# Revit family: SW17 TETT
name_source: partatom
category: Detail Items
units: mm (PartAtom-declared; Revit-internal decimal feet)

## family parameters
Rotate with component = No
Section Shape = Not Defined
Shared = No

## types (5) — shared parameters
URL = www.superwood.dk

## per-type parameters (varying)
| type | b | h | skulder afstand | skulder afstand 2 |
| SW17 TETT 4" - 27x95mm | 27 mm | 95 mm | 13 mm | 13 mm |
| SW17 TETT 6" - 21x145mm | 21 mm | 145 mm  [stored 0.475722 ft] | 15 mm  [stored 0.0492126 ft] | 15 mm  [stored 0.0492126 ft] |
| SW17 TETT 5" - 21x120mm | 21 mm | 120 mm | 15 mm  [stored 0.0492126 ft] | 15 mm  [stored 0.0492126 ft] |
| SW17 TETT 4" - 21x95mm | 21 mm | 95 mm | 13 mm | 13 mm |
| SW17 TETT 3" - 21x70mm | 21 mm | 70 mm | 13 mm | 13 mm |

note: [stored X ft] marks values corroborated as IEEE doubles in the binary element streams (Revit-internal decimal feet)

## geometry (parser evidence)
native form markers: Sweep x2
no freeform markers — native parametric forms only
